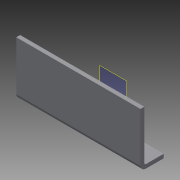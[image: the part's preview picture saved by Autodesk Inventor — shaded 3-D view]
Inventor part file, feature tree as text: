
AUTODESK INVENTOR PART (.ipt)
format: ipt  version: 2013 (Build 170138000, 138)  size: 138,752 bytes
history: native  units: in
note: dims shown in document units (in); Inventor stores cm internally (conversion verified against a paired STEP export)
features: sheet_metal_op x6, sketch x6, other x6, reference x2, plane x1
ambient origin geometry x8: Origin, YZ Plane, XZ Plane, XY Plane, X Axis, Y Axis, Z Axis, Center Point
bodies: Solid1 (feature_tree)
feature tree (21):
  sheet_metal_op  "Face1"
  plane  "Work Plane1"
  sheet_metal_op  "Flange2"
  sheet_metal_op  "Face2"
  sketch  "Sketch1"  dims[d2=0.266in d3=0.266in]
  other  "Plate1"
  sketch  "Sketch4"  dims[d9=0.125in]
  other  "Plate3"
  sheet_metal_op  "Bend2"
  sheet_metal_op  "Corner2"
  sketch  "Sketch5"  dims[d26=0.75in]
  sketch  "Sketch6"  dims[d27=4.0in]
  other  "Plate4"
  sheet_metal_op  "Bend3"
  sketch  "Sketch7"  dims[d28=0.125in]
  reference  "Reference1"
  reference  "Reference2"
  sketch  "Sketch8"  dims[d29=0.0625in d30=0.25in d31=0.125in d32=1.75in d33=90.0deg d34=0.05in d35=0.5in d36=0.125in d37=0.125in d42=0.25in d43=0.125in d44=0.0in d45=0.125in d46=0.125in d47=0.0625in d48=0.25in d49=0.125in d50=0.125in d51=0.0in d52=1.125in d53=0.125in d54=0.0in]
  other  "Cut3"
  other  "Cut4"
  other  "Cut5"
